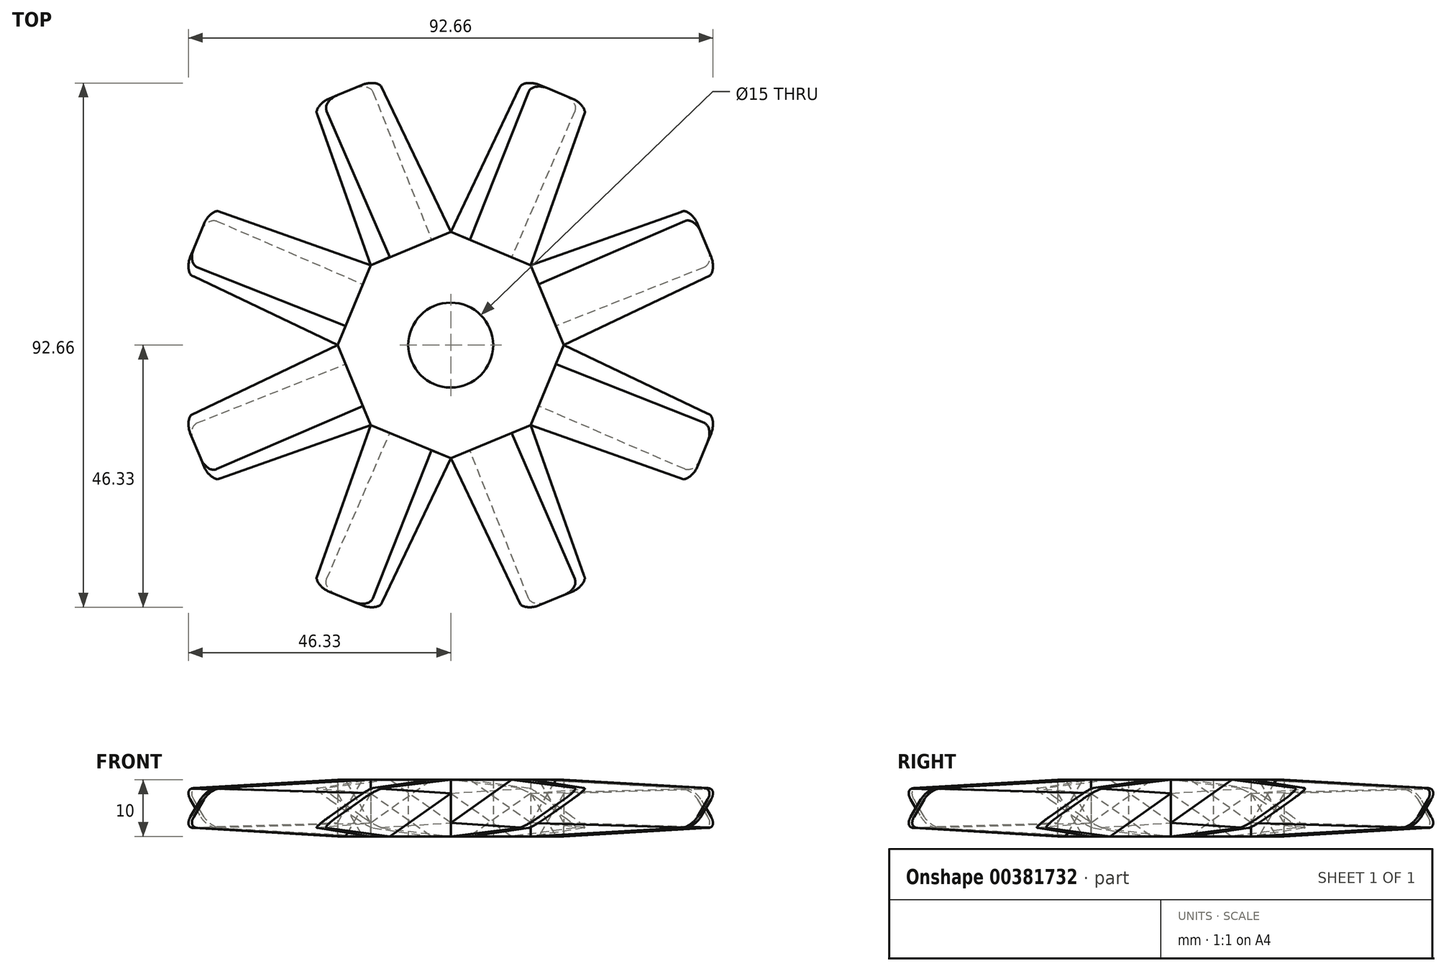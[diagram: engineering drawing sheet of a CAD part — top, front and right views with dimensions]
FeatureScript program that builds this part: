
annotation { "Feature Type Name" : "Feature", "Feature Type Description" : "" }
export const myFeature = defineFeature(function(context is Context, id is Id, definition is map)
    precondition{}
    {
        {
            var Q0;
            Q0=qCreatedBy(makeId("Top.planeOp"),FACE);
            var sketch = newSketch(context, id + "F0", { "sketchPlane" : qUnion([Q0])});
            skCircle(sketch, "E0", {"center": v(0, 0) * mm, "radius": 20 * mm, "construction": true});
            skLineSegment(sketch, "E1", {"start": v(0, 0) * mm, "end": v(0, 20) * mm, "construction": true});
            skCircle(sketch, "E2", {"center": v(0, 0) * mm, "radius": 10 * mm, "construction": true});
            skLineSegment(sketch, "E3", {"start": v(-10, 0) * mm, "end": v(-20, 0) * mm});
            skLineSegment(sketch, "E4.1.0", {"start": v(-7.07, -7.07) * mm, "end": v(-14.14, -14.14) * mm});
            skLineSegment(sketch, "E4.2.0", {"start": v(0, -10) * mm, "end": v(0, -20) * mm});
            skLineSegment(sketch, "E4.3.0", {"start": v(7.07, -7.07) * mm, "end": v(14.14, -14.14) * mm});
            skLineSegment(sketch, "E4.4.0", {"start": v(10, 0) * mm, "end": v(20, 0) * mm});
            skLineSegment(sketch, "E4.5.0", {"start": v(7.07, 7.07) * mm, "end": v(14.14, 14.14) * mm});
            skLineSegment(sketch, "E4.6.0", {"start": v(0, 10) * mm, "end": v(0, 20) * mm});
            skLineSegment(sketch, "E4.7.0", {"start": v(-7.07, 7.07) * mm, "end": v(-14.14, 14.14) * mm});
            skLineSegment(sketch, "E5", {"start": v(-14.14, -14.14) * mm, "end": v(0, -20) * mm});
            skLineSegment(sketch, "E6.1.0", {"start": v(0, -20) * mm, "end": v(14.14, -14.14) * mm});
            skLineSegment(sketch, "E6.2.0", {"start": v(14.14, -14.14) * mm, "end": v(20, 0) * mm});
            skLineSegment(sketch, "E6.3.0", {"start": v(20, 0) * mm, "end": v(14.14, 14.14) * mm});
            skLineSegment(sketch, "E6.4.0", {"start": v(14.14, 14.14) * mm, "end": v(0, 20) * mm});
            skLineSegment(sketch, "E6.5.0", {"start": v(0, 20) * mm, "end": v(-14.14, 14.14) * mm});
            skLineSegment(sketch, "E6.6.0", {"start": v(-14.14, 14.14) * mm, "end": v(-20, 0) * mm});
            skLineSegment(sketch, "E6.7.0", {"start": v(-20, 0) * mm, "end": v(-14.14, -14.14) * mm});
            skSolve(sketch);
        }
        {
            var Q0;
            Q0=makeQuery(id+"F0.imprint","IMPRINT",FACE,{"disambiguationData":[TD([[makeQuery(id+"F0.imprint","IMPRINT",EDGE,{"derivedFrom":sQuery(id+"F0.wireOp",EDGE,"E5")}),1.0]])]});
            extrude(context, id + "F1", {"entities" : qUnion([Q0]), "depth" : 10 * mm});
        }
        {
            var Q0;
            Q0=makeQuery(id+"F1.opExtrude","SWEPT_FACE",FACE,{"disambiguationData":[OSD([sQuery(id+"F0.wireOp",EDGE,"E6.3.0")])]});
            var sketch = newSketch(context, id + "F2", { "sketchPlane" : qUnion([Q0])});
            skLineSegment(sketch, "E7", {"start": v(7.65, 10) * mm, "end": v(-7.65, 0) * mm, "construction": true});
            skLineSegment(sketch, "E8", {"start": v(-7.65, 10) * mm, "end": v(7.65, 0) * mm, "construction": true});
            skLineSegment(sketch, "E9", {"start": v(4, 10) * mm, "end": v(-7.65, 2.39) * mm});
            skLineSegment(sketch, "E10", {"start": v(-4, 0) * mm, "end": v(7.65, 7.61) * mm});
            skSolve(sketch);
        }
        {
            var Q0;
            {var subQ4=sQuery(id+"F2.wireOp",EDGE,"E9");Q0=makeQuery(id+"F2.imprint","IMPRINT",FACE,{"disambiguationData":[TD([[makeQuery(id+"F2.imprint","IMPRINT",EDGE,{"derivedFrom":subQ4}),1.0]])]});}
            extrude(context, id + "F3", {"entities" : qUnion([Q0]), "depth" : 30 * mm, "hasDraft" : true, "draftAngle" : 3 * degree, "draftPullDirection" : true});
        }
        {
            var Q0;
            Q0=makeQuery(id+"F1.opExtrude","CAP_FACE",FACE,{"disambiguationData":[OSD([sQuery(id+"F0.wireOp",EDGE,"E5"),sQuery(id+"F0.wireOp",EDGE,"E6.1.0"),sQuery(id+"F0.wireOp",EDGE,"E6.2.0"),sQuery(id+"F0.wireOp",EDGE,"E6.3.0"),sQuery(id+"F0.wireOp",EDGE,"E6.4.0"),sQuery(id+"F0.wireOp",EDGE,"E6.5.0"),sQuery(id+"F0.wireOp",EDGE,"E6.6.0"),sQuery(id+"F0.wireOp",EDGE,"E6.7.0")])],"isStart":false});
            var sketch = newSketch(context, id + "F4", { "sketchPlane" : qUnion([Q0])});
            skLineSegment(sketch, "E11", {"start": v(14.14, -14.14) * mm, "end": v(-14.14, 14.14) * mm, "construction": true});
            skLineSegment(sketch, "E12", {"start": v(-14.14, -14.14) * mm, "end": v(14.14, 14.14) * mm, "construction": true});
            skCircle(sketch, "E13", {"center": v(0, 0) * mm, "radius": 5 * mm});
            skSolve(sketch);
        }
        {
            var Q0;
            Q0=makeQuery(id+"F3.opExtrude","SWEPT_BODY",BODY,{"disambiguationData":[OSD([sQuery(id+"F0.wireOp",EDGE,"E6.2.0"),sQuery(id+"F0.wireOp",EDGE,"E6.3.0"),sQuery(id+"F0.wireOp",EDGE,"E6.4.0"),sQuery(id+"F2.wireOp",EDGE,"E9"),sQuery(id+"F2.wireOp",EDGE,"E10")])]});
            var Q1;
            Q1=sQuery(id+"F4.wireOp",EDGE,"E13");
            circularPattern(context, id + "F5", {"entities" : qUnion([Q0]), "axis" : qUnion([Q1]), "angle" : 360 * degree, "instanceCount" : 8, "oppositeDirection" : true, "equalSpace" : true});
        }
        {
            var Q0;
            Q0=makeQuery(id+"F1.opExtrude","CAP_FACE",FACE,{"disambiguationData":[OSD([sQuery(id+"F0.wireOp",EDGE,"E5"),sQuery(id+"F0.wireOp",EDGE,"E6.1.0"),sQuery(id+"F0.wireOp",EDGE,"E6.2.0"),sQuery(id+"F0.wireOp",EDGE,"E6.3.0"),sQuery(id+"F0.wireOp",EDGE,"E6.4.0"),sQuery(id+"F0.wireOp",EDGE,"E6.5.0"),sQuery(id+"F0.wireOp",EDGE,"E6.6.0"),sQuery(id+"F0.wireOp",EDGE,"E6.7.0")])],"isStart":true});
            var sketch = newSketch(context, id + "F6", { "sketchPlane" : qUnion([Q0])});
            skLineSegment(sketch, "E14", {"start": v(14.14, 14.14) * mm, "end": v(-14.14, -14.14) * mm, "construction": true});
            skLineSegment(sketch, "E15", {"start": v(14.14, -14.14) * mm, "end": v(-14.14, 14.14) * mm, "construction": true});
            skCircle(sketch, "E16", {"center": v(0, 0) * mm, "radius": 7.5 * mm});
            skSolve(sketch);
        }
        {
            var Q0;
            Q0=makeQuery(id+"F6.imprint","IMPRINT",FACE,{"disambiguationData":[TD([[makeQuery(id+"F6.imprint","IMPRINT",EDGE,{"derivedFrom":sQuery(id+"F6.wireOp",EDGE,"E16")}),1.0]])]});
            var Q1;
            Q1=sQuery(id+"F6.wireOp",EDGE,"E16");
            extrude(context, id + "F7", {"entities" : qUnion([Q0]), "operationType" : NewBodyOperationType.REMOVE, "surfaceEntities" : qUnion([Q1]), "oppositeDirection" : true, "depth" : 25 * mm});
        }
        {
            var Q0;
            {var subQ0=sQuery(id+"F0.wireOp",EDGE,"E6.3.0");var subQ1=makeQuery(id+"F1.opExtrude","CAP_EDGE",EDGE,{"disambiguationData":[OSD([subQ0])],"isStart":true});Q0=makeQuery(id+"F5.opPattern","COPY",EDGE,{"derivedFrom":makeQuery(id+"F3.opExtrude","CAP_EDGE",EDGE,{"disambiguationData":[OSD([subQ0]),TDD([makeQuery(id+"F2.imprint","IMPRINT",EDGE,{"disambiguationData":[TD([[makeQuery(id+"F2.imprint","INTERSECT",VERTEX,{"derivedFrom":[subQ1,sQuery(id+"F2.wireOp",EDGE,"E10")]}),1.0]])],"derivedFrom":subQ1})])],"isStart":false}),"instanceName":"3"});}
            var Q1;
            {var subQ0=sQuery(id+"F0.wireOp",EDGE,"E6.3.0");var subQ1=makeQuery(id+"F1.opExtrude","CAP_EDGE",EDGE,{"disambiguationData":[OSD([subQ0])],"isStart":false});Q1=makeQuery(id+"F5.opPattern","COPY",EDGE,{"derivedFrom":makeQuery(id+"F3.opExtrude","CAP_EDGE",EDGE,{"disambiguationData":[OSD([subQ0]),TDD([makeQuery(id+"F2.imprint","IMPRINT",EDGE,{"disambiguationData":[TD([[makeQuery(id+"F2.imprint","INTERSECT",VERTEX,{"derivedFrom":[subQ1,sQuery(id+"F2.wireOp",EDGE,"E9")]}),-1.0]])],"derivedFrom":subQ1})])],"isStart":false}),"instanceName":"3"});}
            var Q2;
            {var subQ0=sQuery(id+"F0.wireOp",EDGE,"E6.3.0");var subQ1=makeQuery(id+"F1.opExtrude","CAP_EDGE",EDGE,{"disambiguationData":[OSD([subQ0])],"isStart":false});Q2=makeQuery(id+"F5.opPattern","COPY",EDGE,{"derivedFrom":makeQuery(id+"F3.opExtrude","CAP_EDGE",EDGE,{"disambiguationData":[OSD([subQ0]),TDD([makeQuery(id+"F2.imprint","IMPRINT",EDGE,{"disambiguationData":[TD([[makeQuery(id+"F2.imprint","INTERSECT",VERTEX,{"derivedFrom":[subQ1,sQuery(id+"F2.wireOp",EDGE,"E9")]}),-1.0]])],"derivedFrom":subQ1})])],"isStart":false}),"instanceName":"4"});}
            var Q3;
            {var subQ0=sQuery(id+"F0.wireOp",EDGE,"E6.3.0");var subQ1=makeQuery(id+"F1.opExtrude","CAP_EDGE",EDGE,{"disambiguationData":[OSD([subQ0])],"isStart":true});Q3=makeQuery(id+"F5.opPattern","COPY",EDGE,{"derivedFrom":makeQuery(id+"F3.opExtrude","CAP_EDGE",EDGE,{"disambiguationData":[OSD([subQ0]),TDD([makeQuery(id+"F2.imprint","IMPRINT",EDGE,{"disambiguationData":[TD([[makeQuery(id+"F2.imprint","INTERSECT",VERTEX,{"derivedFrom":[subQ1,sQuery(id+"F2.wireOp",EDGE,"E10")]}),1.0]])],"derivedFrom":subQ1})])],"isStart":false}),"instanceName":"4"});}
            var Q4;
            {var subQ0=sQuery(id+"F0.wireOp",EDGE,"E6.3.0");var subQ1=makeQuery(id+"F1.opExtrude","CAP_EDGE",EDGE,{"disambiguationData":[OSD([subQ0])],"isStart":false});Q4=makeQuery(id+"F5.opPattern","COPY",EDGE,{"derivedFrom":makeQuery(id+"F3.opExtrude","CAP_EDGE",EDGE,{"disambiguationData":[OSD([subQ0]),TDD([makeQuery(id+"F2.imprint","IMPRINT",EDGE,{"disambiguationData":[TD([[makeQuery(id+"F2.imprint","INTERSECT",VERTEX,{"derivedFrom":[subQ1,sQuery(id+"F2.wireOp",EDGE,"E9")]}),-1.0]])],"derivedFrom":subQ1})])],"isStart":false}),"instanceName":"5"});}
            var Q5;
            {var subQ0=sQuery(id+"F0.wireOp",EDGE,"E6.3.0");var subQ1=makeQuery(id+"F1.opExtrude","CAP_EDGE",EDGE,{"disambiguationData":[OSD([subQ0])],"isStart":true});Q5=makeQuery(id+"F5.opPattern","COPY",EDGE,{"derivedFrom":makeQuery(id+"F3.opExtrude","CAP_EDGE",EDGE,{"disambiguationData":[OSD([subQ0]),TDD([makeQuery(id+"F2.imprint","IMPRINT",EDGE,{"disambiguationData":[TD([[makeQuery(id+"F2.imprint","INTERSECT",VERTEX,{"derivedFrom":[subQ1,sQuery(id+"F2.wireOp",EDGE,"E10")]}),1.0]])],"derivedFrom":subQ1})])],"isStart":false}),"instanceName":"5"});}
            var Q6;
            {var subQ0=sQuery(id+"F0.wireOp",EDGE,"E6.3.0");var subQ1=makeQuery(id+"F1.opExtrude","CAP_EDGE",EDGE,{"disambiguationData":[OSD([subQ0])],"isStart":true});Q6=makeQuery(id+"F5.opPattern","COPY",EDGE,{"derivedFrom":makeQuery(id+"F3.opExtrude","CAP_EDGE",EDGE,{"disambiguationData":[OSD([subQ0]),TDD([makeQuery(id+"F2.imprint","IMPRINT",EDGE,{"disambiguationData":[TD([[makeQuery(id+"F2.imprint","INTERSECT",VERTEX,{"derivedFrom":[subQ1,sQuery(id+"F2.wireOp",EDGE,"E10")]}),1.0]])],"derivedFrom":subQ1})])],"isStart":false}),"instanceName":"6"});}
            var Q7;
            {var subQ0=sQuery(id+"F0.wireOp",EDGE,"E6.3.0");var subQ1=makeQuery(id+"F1.opExtrude","CAP_EDGE",EDGE,{"disambiguationData":[OSD([subQ0])],"isStart":false});Q7=makeQuery(id+"F5.opPattern","COPY",EDGE,{"derivedFrom":makeQuery(id+"F3.opExtrude","CAP_EDGE",EDGE,{"disambiguationData":[OSD([subQ0]),TDD([makeQuery(id+"F2.imprint","IMPRINT",EDGE,{"disambiguationData":[TD([[makeQuery(id+"F2.imprint","INTERSECT",VERTEX,{"derivedFrom":[subQ1,sQuery(id+"F2.wireOp",EDGE,"E9")]}),-1.0]])],"derivedFrom":subQ1})])],"isStart":false}),"instanceName":"6"});}
            var Q8;
            {var subQ0=sQuery(id+"F0.wireOp",EDGE,"E6.3.0");var subQ1=makeQuery(id+"F1.opExtrude","CAP_EDGE",EDGE,{"disambiguationData":[OSD([subQ0])],"isStart":false});Q8=makeQuery(id+"F5.opPattern","COPY",EDGE,{"derivedFrom":makeQuery(id+"F3.opExtrude","CAP_EDGE",EDGE,{"disambiguationData":[OSD([subQ0]),TDD([makeQuery(id+"F2.imprint","IMPRINT",EDGE,{"disambiguationData":[TD([[makeQuery(id+"F2.imprint","INTERSECT",VERTEX,{"derivedFrom":[subQ1,sQuery(id+"F2.wireOp",EDGE,"E9")]}),-1.0]])],"derivedFrom":subQ1})])],"isStart":false}),"instanceName":"7"});}
            var Q9;
            {var subQ0=sQuery(id+"F0.wireOp",EDGE,"E6.3.0");var subQ1=makeQuery(id+"F1.opExtrude","CAP_EDGE",EDGE,{"disambiguationData":[OSD([subQ0])],"isStart":true});Q9=makeQuery(id+"F5.opPattern","COPY",EDGE,{"derivedFrom":makeQuery(id+"F3.opExtrude","CAP_EDGE",EDGE,{"disambiguationData":[OSD([subQ0]),TDD([makeQuery(id+"F2.imprint","IMPRINT",EDGE,{"disambiguationData":[TD([[makeQuery(id+"F2.imprint","INTERSECT",VERTEX,{"derivedFrom":[subQ1,sQuery(id+"F2.wireOp",EDGE,"E10")]}),1.0]])],"derivedFrom":subQ1})])],"isStart":false}),"instanceName":"7"});}
            var Q10;
            {var subQ0=sQuery(id+"F0.wireOp",EDGE,"E6.3.0");var subQ1=makeQuery(id+"F1.opExtrude","CAP_EDGE",EDGE,{"disambiguationData":[OSD([subQ0])],"isStart":false});Q10=makeQuery(id+"F3.opExtrude","CAP_EDGE",EDGE,{"disambiguationData":[OSD([subQ0]),TDD([makeQuery(id+"F2.imprint","IMPRINT",EDGE,{"disambiguationData":[TD([[makeQuery(id+"F2.imprint","INTERSECT",VERTEX,{"derivedFrom":[subQ1,sQuery(id+"F2.wireOp",EDGE,"E9")]}),-1.0]])],"derivedFrom":subQ1})])],"isStart":false});}
            var Q11;
            {var subQ0=sQuery(id+"F0.wireOp",EDGE,"E6.3.0");var subQ1=makeQuery(id+"F1.opExtrude","CAP_EDGE",EDGE,{"disambiguationData":[OSD([subQ0])],"isStart":true});Q11=makeQuery(id+"F3.opExtrude","CAP_EDGE",EDGE,{"disambiguationData":[OSD([subQ0]),TDD([makeQuery(id+"F2.imprint","IMPRINT",EDGE,{"disambiguationData":[TD([[makeQuery(id+"F2.imprint","INTERSECT",VERTEX,{"derivedFrom":[subQ1,sQuery(id+"F2.wireOp",EDGE,"E10")]}),1.0]])],"derivedFrom":subQ1})])],"isStart":false});}
            var Q12;
            {var subQ0=sQuery(id+"F0.wireOp",EDGE,"E6.3.0");var subQ1=makeQuery(id+"F1.opExtrude","CAP_EDGE",EDGE,{"disambiguationData":[OSD([subQ0])],"isStart":false});Q12=makeQuery(id+"F5.opPattern","COPY",EDGE,{"derivedFrom":makeQuery(id+"F3.opExtrude","CAP_EDGE",EDGE,{"disambiguationData":[OSD([subQ0]),TDD([makeQuery(id+"F2.imprint","IMPRINT",EDGE,{"disambiguationData":[TD([[makeQuery(id+"F2.imprint","INTERSECT",VERTEX,{"derivedFrom":[subQ1,sQuery(id+"F2.wireOp",EDGE,"E9")]}),-1.0]])],"derivedFrom":subQ1})])],"isStart":false}),"instanceName":"1"});}
            var Q13;
            {var subQ0=sQuery(id+"F0.wireOp",EDGE,"E6.3.0");var subQ1=makeQuery(id+"F1.opExtrude","CAP_EDGE",EDGE,{"disambiguationData":[OSD([subQ0])],"isStart":true});Q13=makeQuery(id+"F5.opPattern","COPY",EDGE,{"derivedFrom":makeQuery(id+"F3.opExtrude","CAP_EDGE",EDGE,{"disambiguationData":[OSD([subQ0]),TDD([makeQuery(id+"F2.imprint","IMPRINT",EDGE,{"disambiguationData":[TD([[makeQuery(id+"F2.imprint","INTERSECT",VERTEX,{"derivedFrom":[subQ1,sQuery(id+"F2.wireOp",EDGE,"E10")]}),1.0]])],"derivedFrom":subQ1})])],"isStart":false}),"instanceName":"1"});}
            var Q14;
            {var subQ0=sQuery(id+"F0.wireOp",EDGE,"E6.3.0");var subQ1=makeQuery(id+"F1.opExtrude","CAP_EDGE",EDGE,{"disambiguationData":[OSD([subQ0])],"isStart":true});Q14=makeQuery(id+"F5.opPattern","COPY",EDGE,{"derivedFrom":makeQuery(id+"F3.opExtrude","CAP_EDGE",EDGE,{"disambiguationData":[OSD([subQ0]),TDD([makeQuery(id+"F2.imprint","IMPRINT",EDGE,{"disambiguationData":[TD([[makeQuery(id+"F2.imprint","INTERSECT",VERTEX,{"derivedFrom":[subQ1,sQuery(id+"F2.wireOp",EDGE,"E10")]}),1.0]])],"derivedFrom":subQ1})])],"isStart":false}),"instanceName":"2"});}
            var Q15;
            {var subQ0=sQuery(id+"F0.wireOp",EDGE,"E6.3.0");var subQ1=makeQuery(id+"F1.opExtrude","CAP_EDGE",EDGE,{"disambiguationData":[OSD([subQ0])],"isStart":false});Q15=makeQuery(id+"F5.opPattern","COPY",EDGE,{"derivedFrom":makeQuery(id+"F3.opExtrude","CAP_EDGE",EDGE,{"disambiguationData":[OSD([subQ0]),TDD([makeQuery(id+"F2.imprint","IMPRINT",EDGE,{"disambiguationData":[TD([[makeQuery(id+"F2.imprint","INTERSECT",VERTEX,{"derivedFrom":[subQ1,sQuery(id+"F2.wireOp",EDGE,"E9")]}),-1.0]])],"derivedFrom":subQ1})])],"isStart":false}),"instanceName":"2"});}
            fillet(context, id + "F8", {"entities" : qUnion([Q0, Q1, Q2, Q3, Q4, Q5, Q6, Q7, Q8, Q9, Q10, Q11, Q12, Q13, Q14, Q15]), "radius" : 2 * mm, "tangentPropagation" : true, "allowEdgeOverflow" : false});
        }
    });
